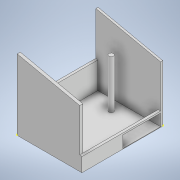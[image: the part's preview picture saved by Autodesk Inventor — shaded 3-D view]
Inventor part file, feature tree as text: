
AUTODESK INVENTOR PART (.ipt)
format: ipt  version: 2022 (Build 260153000, 153)  size: 178,688 bytes
history: native  units: in
note: dims shown in document units (in); Inventor stores cm internally (conversion verified against a paired STEP export)
features: sketch x15, extrude x10
ambient origin geometry x8: Origin, YZ Plane, XZ Plane, XY Plane, X Axis, Y Axis, Z Axis, Center Point
bodies: Solid1 (feature_tree)
feature tree (25):
  extrude  "Extrusion1"  Depth=14.4in
  extrude  "Extrusion2"  Depth=18.0in TaperAngle=0.0deg
  extrude  "Extrusion3"  Depth=18.0in TaperAngle=0.0deg
  sketch  "Sketch4"  dims[d11=1.2in d12=0.0in d13=10.8in d14=0.0in]
  extrude  "Extrusion4"  Depth=10.8in TaperAngle=0.0deg
  sketch  "Sketch6"  dims[d18=120.0in d19=0.0in d20=15.6in d21=0.0in]
  extrude  "Extrusion5"  Depth=3.0in
  sketch  "Sketch8"  dims[d25=8.4in d26=0.36in]
  extrude  "Extrusion6"  Depth=15.6in TaperAngle=0.0deg
  extrude  "Extrusion7"  Depth=0.6in
  extrude  "Extrusion8"  Depth=8.4in
  extrude  "Extrusion9"  Depth=8.4in TaperAngle=0.0deg
  sketch  "Sketch13"
  sketch  "Sketch14"
  extrude  "Extrusion10"  [1 undecoded]
  sketch  "Sketch1"  dims[d0=6.0in d1=14.4in]
  sketch  "Sketch2"  dims[d2=18.0in d3=0.0in d4=16.8in d5=0.0in]
  sketch  "Sketch3"  dims[d6=0.12in d7=18.0in d8=0.0in]
  sketch  "Sketch5"  dims[d15=15.6in d16=0.0in d17=3.0in]
  sketch  "Sketch7"  dims[d22=120.0in d23=0.0in d24=0.6in]
  sketch  "Sketch9"  dims[d27=8.4in d28=1.0in d29=0.0in]
  sketch  "Sketch10"
  sketch  "Sketch11"
  sketch  "Sketch12"
  sketch  "Sketch15"
note: 1 required parameter value undecoded (feature->parameter linkage not recoverable at this tier; creation-order binding heuristic only, values carry confidence <= 0.55)
